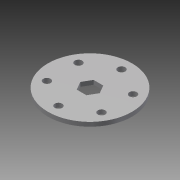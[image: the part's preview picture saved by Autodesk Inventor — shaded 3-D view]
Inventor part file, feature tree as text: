
AUTODESK INVENTOR PART (.ipt)
format: ipt  version: 2013 (Build 170138000, 138)  size: 95,744 bytes
history: native  units: in
note: dims shown in document units (in); Inventor stores cm internally (conversion verified against a paired STEP export)
features: extrude x1, sketch x1
ambient origin geometry x8: Origin, YZ Plane, XZ Plane, XY Plane, X Axis, Y Axis, Z Axis, Center Point
feature tree (2):
  extrude  "Extrusion3"  Depth=0.22in
  sketch  "Sketch1"  dims[d0=0.375in d5=0.22in d7=2.3622in d9=360.0deg d22=0.5in d23=0.125in d24=0.0in]
